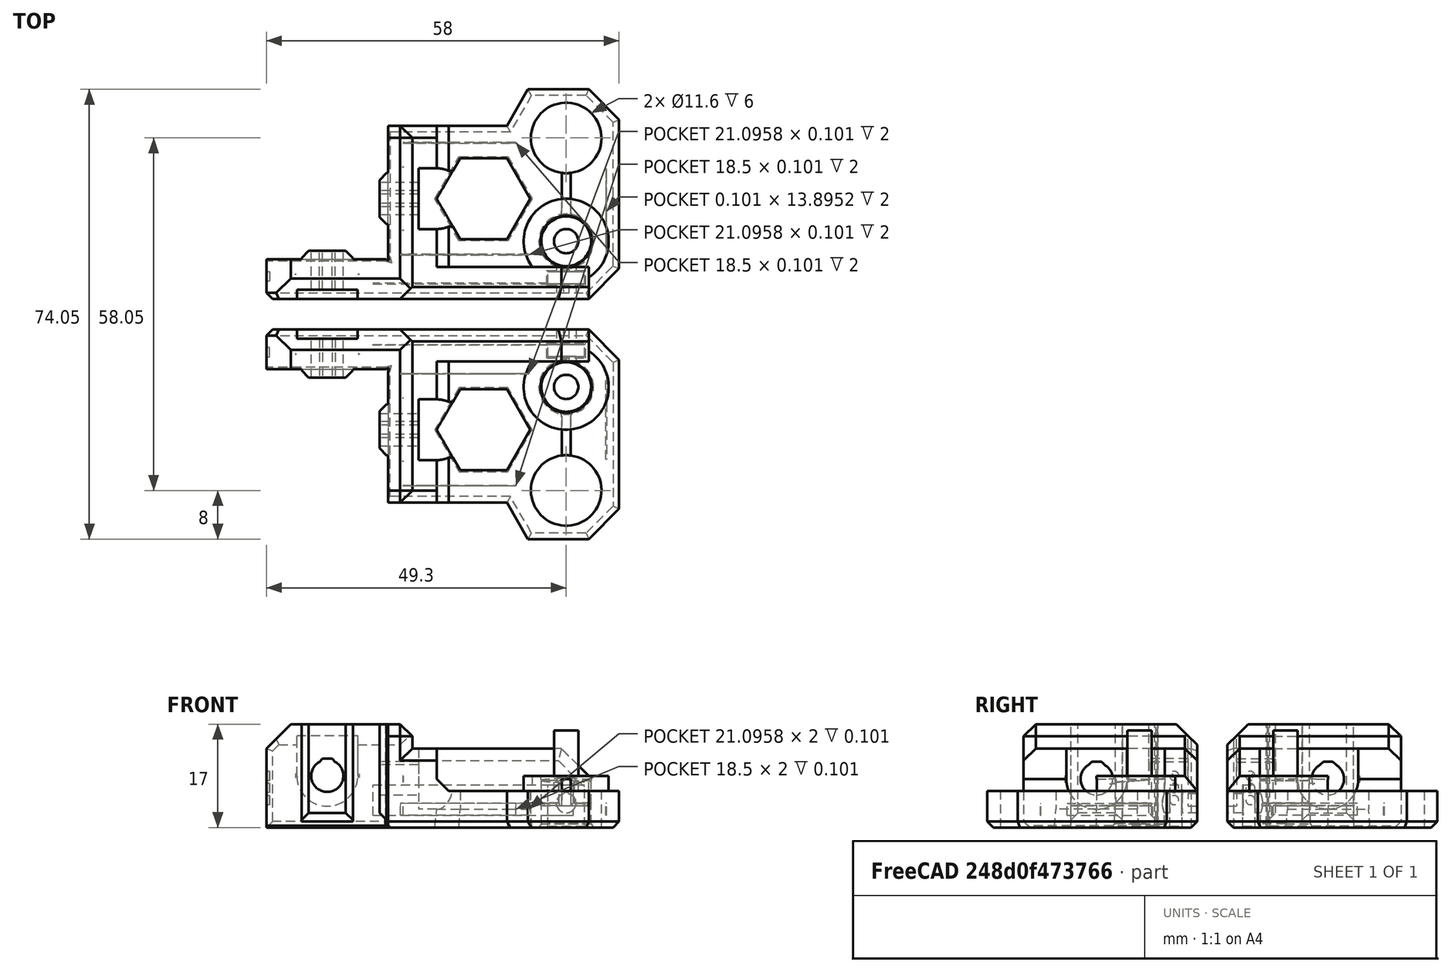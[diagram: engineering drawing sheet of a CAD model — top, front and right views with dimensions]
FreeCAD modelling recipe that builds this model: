
FCSTD DOCUMENT  (FreeCAD 0.18R14555 (Git shallow))
Label: bear-z-tops-with-rod-stopper
License: All rights reserved
LicenseURL: http://en.wikipedia.org/wiki/All_rights_reserved
objects: Part::Cylinder×10, Part::Cut×10, Part::Box×2, Part::Feature×2, App::Part×2, Part::Chamfer×2
note: 26 computed .brp shape members not serialized (recipe doc carries the construction recipe); baked Part::Feature solids carry a one-line shape summary decoded from their .brp

FEATURE [Part::Box] Box  label="square-nut-1"
  AttacherType = Attacher::AttachEngine3D
  Height = 7
  Length = 6
  Placement = pos=(-3,-7,-6) rot=(0,0,1;0rad)
  Width = 2
FEATURE [Part::Cylinder] Cylinder
  Angle = 360
  AttacherType = Attacher::AttachEngine3D
  Height = 10
  Radius = 2
FEATURE [Part::Cylinder] Cylinder001
  Angle = 360
  AttacherType = Attacher::AttachEngine3D
  Height = 10
  Placement = pos=(0,-24,0) rot=(0,0,1;0rad)
  Radius = 2
FEATURE [Part::Box] Box001  label="square-nut-2"
  AttacherType = Attacher::AttachEngine3D
  Height = 7
  Length = 6
  Placement = pos=(-3,-19,-6) rot=(0,0,1;0rad)
  Width = 2
FEATURE [Part::Cylinder] Cylinder002  label="rod-cut-1"
  Angle = 360
  AttacherType = Attacher::AttachEngine3D
  Height = 10
  Placement = pos=(0,-24,-6) rot=(0,0,1;0rad)
  Radius = 4
FEATURE [Part::Cylinder] Cylinder003  label="rod-cut-2"
  Angle = 360
  AttacherType = Attacher::AttachEngine3D
  Height = 10
  Placement = pos=(0,0,-6) rot=(0,0,1;0rad)
  Radius = 4
FEATURE [Part::Feature] Part__Feature  label="z_top"
  shape: bbox 58 x 34.53 x 17 mm, 162 faces (baked)
FEATURE [Part::Feature] Part__Feature001  label="z_top(Mirror)"
  Placement = pos=(-1.8e-14,-24.05,0) rot=(1,0,0;3.14159rad)
  shape: bbox 58 x 34.53 x 17 mm, 162 faces (baked)
FEATURE [App::Part] z_tops
  Group = -> [Part__Feature,Part__Feature001]
  Origin = -> Origin
FEATURE [App::Part] z_top_v11  label="z_top v11"
  Group = -> [z_tops]
  Origin = -> Origin001
FEATURE [Part::Cut] Cut
  Base = -> Part__Feature001
  Tool = -> Cylinder002
FEATURE [Part::Cut] Cut001
  Base = -> Part__Feature
  Tool = -> Cylinder003
FEATURE [Part::Cylinder] Cylinder004  label="Cylinder002"
  Angle = 360
  AttacherType = Attacher::AttachEngine3D
  Height = 23
  Placement = pos=(0,0,-2) rot=(1,0,0;1.5708rad)
  Radius = 1.6
FEATURE [Part::Cylinder] Cylinder005  label="Cylinder003"
  Angle = 360
  AttacherType = Attacher::AttachEngine3D
  Height = 23
  Placement = pos=(0,0,-2) rot=(1,0,0;1.5708rad)
  Radius = 1.6
FEATURE [Part::Cut] Cut002
  Base = -> Cut001
  Tool = -> Cylinder004
FEATURE [Part::Cut] Cut003
  Base = -> Cut
  Tool = -> Cylinder005
FEATURE [Part::Cut] Cut004
  Base = -> Cut002
  Tool = -> Box
FEATURE [Part::Cut] Cut005
  Base = -> Cut003
  Tool = -> Box001
FEATURE [Part::Cylinder] Cylinder006  label="Cylinder004"
  Angle = 360
  AttacherType = Attacher::AttachEngine3D
  Height = 23
  Placement = pos=(0,-2e-16,-0.7) rot=(1,0,0;1.5708rad)
  Radius = 0.5
FEATURE [Part::Cylinder] Cylinder007  label="Cylinder005"
  Angle = 360
  AttacherType = Attacher::AttachEngine3D
  Height = 23
  Placement = pos=(0,-2e-16,-0.7) rot=(1,0,0;1.5708rad)
  Radius = 0.5
FEATURE [Part::Cut] Cut006
  Base = -> Cut005
  Tool = -> Cylinder006
FEATURE [Part::Cut] Cut007
  Base = -> Cut004
  Tool = -> Cylinder007
FEATURE [Part::Chamfer] Chamfer
  Base = -> Cut007
  Edges = 4 edges r=0.2: [Edge29,Edge30,Edge31,Edge32]
FEATURE [Part::Chamfer] Chamfer001
  Base = -> Cut006
  Edges = 4 edges r=0.2: [Edge29,Edge30,Edge31,Edge32]
FEATURE [Part::Cylinder] Cylinder008  label="extra-hole-dia"
  Angle = 360
  AttacherType = Attacher::AttachEngine3D
  Height = 10
  Placement = pos=(0,0,-6.7) rot=(0,0,1;0rad)
  Radius = 4.1
FEATURE [Part::Cylinder] Cylinder009  label="extra-hole-dia001"
  Angle = 360
  AttacherType = Attacher::AttachEngine3D
  Height = 10
  Placement = pos=(0,-24,-6.7) rot=(0,0,1;0rad)
  Radius = 4.1
FEATURE [Part::Cut] Cut008
  Base = -> Chamfer001
  Tool = -> Cylinder009
FEATURE [Part::Cut] Cut009
  Base = -> Chamfer
  Tool = -> Cylinder008
